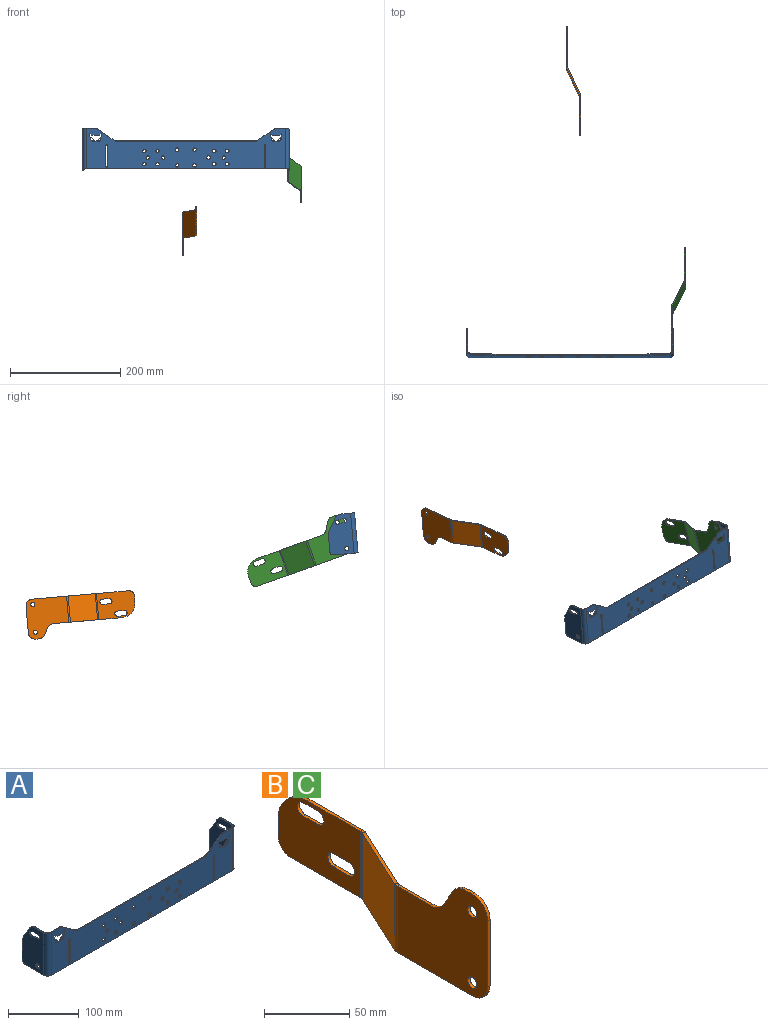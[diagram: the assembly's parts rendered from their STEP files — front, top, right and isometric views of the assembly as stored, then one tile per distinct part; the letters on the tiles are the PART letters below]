
ASSEMBLY  parts=3 mates=1
PART A: 94 faces, bbox 375.8x50.8x73 mm
  f0: cylinder r=4.27mm len=6.04mm, axis (0,-1,0), area 20.5mm2, adj f55,f56,f57
  f1: cylinder r=4.27mm len=6.04mm, axis (0,-1,0), area 20.5mm2, adj f54,f56,f57
  f2: cylinder r=6.35mm len=3.64mm, axis (0,-1,0), area 7.7mm2, adj f3,f53,f56,f57
  f3: plane 28.46x19.93mm, normal (-0.57,0,0.82), area 68.8mm2, adj f2,f4,f56,f57
  f4: cylinder r=6.35mm len=3.64mm, axis (0,-1,0), area 7.7mm2, adj f3,f5,f56,f57
  f5: plane 18.32x1.98mm, normal (0,0,1), area 36.3mm2, adj f4,f56,f57,f72
  f6: plane 361.68x1.98mm, normal (0,0,-1), area 716.6mm2, adj f56,f57,f73,f90
  f7: plane 18.32x1.98mm, normal (0,0,1), area 36.3mm2, adj f8,f56,f57,f91
  f8: cylinder r=6.35mm len=3.64mm, axis (0,-1,0), area 7.7mm2, adj f7,f9,f56,f57
  f9: plane 28.46x19.93mm, normal (0.57,0,0.82), area 68.8mm2, adj f8,f10,f56,f57
  f10: cylinder r=6.35mm len=3.64mm, axis (0,-1,0), area 7.7mm2, adj f9,f53,f56,f57
  f11: plane 5.66x5.66mm, normal (0.71,0,-0.71), area 15.8mm2, adj f36,f56,f57
  f12: plane 5x1.98mm, normal (-1,0,0), area 9.9mm2, adj f13,f35,f56,f57
  f13: plane 3.54x3.54mm, normal (0.71,0,-0.71), area 9.9mm2, adj f12,f14,f56,f57
  f14: plane 14.14x1.98mm, normal (0,0,-1), area 28mm2, adj f13,f15,f56,f57
  f15: plane 3.54x3.54mm, normal (-0.71,0,-0.71), area 9.9mm2, adj f14,f16,f56,f57
  f16: plane 5x1.98mm, normal (1,0,0), area 9.9mm2, adj f15,f17,f56,f57
  f17: plane 10.61x10.61mm, normal (0.71,0,0.71), area 29.7mm2, adj f16,f35,f56,f57
  f18: plane 5.66x5.66mm, normal (0.71,0,-0.71), area 15.8mm2, adj f34,f56,f57
  f19: plane 5x1.98mm, normal (-1,0,0), area 9.9mm2, adj f20,f33,f56,f57
  f20: plane 3.54x3.54mm, normal (0.71,0,-0.71), area 9.9mm2, adj f19,f21,f56,f57
  f21: plane 14.14x1.98mm, normal (0,0,-1), area 28mm2, adj f20,f22,f56,f57
  f22: plane 3.54x3.54mm, normal (-0.71,0,-0.71), area 9.9mm2, adj f21,f23,f56,f57
  f23: plane 5x1.98mm, normal (1,0,0), area 9.9mm2, adj f22,f24,f56,f57
  f24: plane 10.61x10.61mm, normal (0.71,0,0.71), area 29.7mm2, adj f23,f33,f56,f57
  f25: cylinder r=1.59mm len=3.18mm, axis (0,-1,0), area 9.9mm2, adj f26,f32,f56,f57
  f26: plane 38.1x1.98mm, normal (-1,0,0), area 75.5mm2, adj f25,f27,f56,f57
  f27: cylinder r=1.59mm len=3.18mm, axis (0,-1,0), area 9.9mm2, adj f26,f32,f56,f57
  f28: cylinder r=1.59mm len=3.18mm, axis (0,-1,0), area 9.9mm2, adj f29,f31,f56,f57
  f29: plane 38.1x1.98mm, normal (-1,0,0), area 75.5mm2, adj f28,f30,f56,f57
  f30: cylinder r=1.59mm len=3.18mm, axis (0,-1,0), area 9.9mm2, adj f29,f31,f56,f57
  f31: plane 38.1x1.98mm, normal (1,0,0), area 75.5mm2, adj f28,f30,f56,f57
  f32: plane 38.1x1.98mm, normal (1,0,0), area 75.5mm2, adj f25,f27,f56,f57
  f33: plane 10.61x10.61mm, normal (-0.71,0,0.71), area 29.7mm2, adj f19,f24,f56,f57
  f34: cylinder r=4.27mm len=6.04mm, axis (0,-1,0), area 20.5mm2, adj f18,f56,f57
  f35: plane 10.61x10.61mm, normal (-0.71,0,0.71), area 29.7mm2, adj f12,f17,f56,f57
  f36: cylinder r=4.27mm len=6.04mm, axis (0,-1,0), area 20.5mm2, adj f11,f56,f57
  f37: cylinder r=3.17mm len=6.35mm, axis (0,-1,0), area 39.5mm2, adj f56,f57
  f38: cylinder r=3.17mm len=6.35mm, axis (0,-1,0), area 39.5mm2, adj f56,f57
  f39: cylinder r=3.17mm len=6.35mm, axis (0,-1,0), area 39.5mm2, adj f56,f57
  f40: cylinder r=3.17mm len=6.35mm, axis (0,-1,0), area 39.5mm2, adj f56,f57
  f41: cylinder r=3.17mm len=6.35mm, axis (0,-1,0), area 39.5mm2, adj f56,f57
  f42: cylinder r=3.17mm len=6.35mm, axis (0,-1,0), area 39.5mm2, adj f56,f57
  f43: cylinder r=3.17mm len=6.35mm, axis (0,-1,0), area 39.5mm2, adj f56,f57
  f44: cylinder r=3.17mm len=6.35mm, axis (0,-1,0), area 39.5mm2, adj f56,f57
  f45: cylinder r=3.17mm len=6.35mm, axis (0,-1,0), area 39.5mm2, adj f56,f57
  f46: cylinder r=3.17mm len=6.35mm, axis (0,-1,0), area 39.5mm2, adj f56,f57
  f47: cylinder r=3.17mm len=6.35mm, axis (0,-1,0), area 39.5mm2, adj f56,f57
  f48: cylinder r=3.17mm len=6.35mm, axis (0,-1,0), area 39.5mm2, adj f56,f57
  f49: cylinder r=3.17mm len=6.35mm, axis (0,-1,0), area 39.5mm2, adj f56,f57
  f50: cylinder r=3.17mm len=6.35mm, axis (0,-1,0), area 39.5mm2, adj f56,f57
  f51: cylinder r=3.17mm len=6.35mm, axis (0,-1,0), area 39.5mm2, adj f56,f57
  f52: cylinder r=3.17mm len=6.35mm, axis (0,-1,0), area 39.5mm2, adj f56,f57
  f53: plane 253.56x1.98mm, normal (0,0,1), area 502.3mm2, adj f2,f10,f56,f57
  f54: plane 5.66x5.66mm, normal (-0.71,0,-0.71), area 15.8mm2, adj f1,f56,f57
  f55: plane 5.66x5.66mm, normal (-0.71,0,-0.71), area 15.8mm2, adj f0,f56,f57
  f56: plane 361.68x73.03mm, normal (0,1,0), area 18841.1mm2, adj f0,f1,f2,f3,f4,f5,f6,f7
  f57: plane 361.68x73.03mm, normal (0,-1,0), area 18841.1mm2, adj f0,f1,f2,f3,f4,f5,f6,f7
  f58: plane 33.22x1.98mm, normal (0,1,0), area 65.8mm2, adj f67,f68,f69,f70
  f59: plane 37.39x1.98mm, normal (0,0,-1), area 74.1mm2, adj f67,f68,f69,f73
  f60: plane 18.08x1.98mm, normal (0,0,1), area 35.8mm2, adj f67,f68,f71,f72
  f61: cylinder r=3.81mm len=7.42mm, axis (-1,0,0), area 23.8mm2, adj f62,f65,f67,f68
  f62: cylinder r=35.1mm len=14.13mm, axis (-1,0,0), area 28.4mm2, adj f61,f63,f67,f68
  f63: cylinder r=3.81mm len=7.61mm, axis (-1,0,0), area 23.8mm2, adj f62,f65,f67,f68
  f64: cylinder r=3.81mm len=7.62mm, axis (-1,0,0), area 47.4mm2, adj f67,f68
  f65: cylinder r=26.75mm len=11.03mm, axis (-1,0,0), area 22.2mm2, adj f61,f63,f67,f68
  f66: plane 23.93x13.81mm, normal (0,0.87,0.5), area 54.7mm2, adj f67,f68,f70,f71
  f67: plane 73.03x43.74mm, normal (-1,0,0), area 2696.9mm2, adj f58,f59,f60,f61,f62,f63,f64,f65
  f68: plane 73.03x43.74mm, normal (1,0,0), area 2696.9mm2, adj f58,f59,f60,f61,f62,f63,f64,f65
  f69: cylinder r=6.35mm len=6.35mm, axis (-1,0,0), area 19.8mm2, adj f58,f59,f67,f68
  f70: cylinder r=6.35mm len=3.18mm, axis (1,0,0), area 6.6mm2, adj f58,f66,f67,f68
  f71: cylinder r=12.7mm len=11mm, axis (1,0,0), area 26.3mm2, adj f60,f66,f67,f68
  f72: plane 7.06x7.06mm, normal (0,0,1), area 18.9mm2, adj f5,f60,f74,f75
  f73: plane 7.06x7.06mm, normal (0,0,-1), area 18.9mm2, adj f6,f59,f74,f75
  f74: cylinder r=7.06mm len=73.03mm, axis (0,0,1), area 810mm2, adj f57,f68,f72,f73
  f75: cylinder r=5.08mm len=73.03mm, axis (0,0,1), area 582.7mm2, adj f56,f67,f72,f73
  f76: cylinder r=3.81mm len=7.42mm, axis (1,0,0), area 23.8mm2, adj f77,f84,f85,f86
  f77: cylinder r=26.75mm len=11.03mm, axis (1,0,0), area 22.2mm2, adj f76,f78,f85,f86
  f78: cylinder r=3.81mm len=7.61mm, axis (1,0,0), area 23.8mm2, adj f77,f84,f85,f86
  f79: plane 37.39x1.98mm, normal (0,0,-1), area 74.1mm2, adj f85,f86,f87,f90
  f80: plane 33.22x1.98mm, normal (0,1,0), area 65.8mm2, adj f85,f86,f87,f89
  f81: plane 23.93x13.81mm, normal (0,0.87,0.5), area 54.7mm2, adj f85,f86,f88,f89
  f82: plane 18.08x1.98mm, normal (0,0,1), area 35.8mm2, adj f85,f86,f88,f91
  f83: cylinder r=3.81mm len=7.62mm, axis (1,0,0), area 47.4mm2, adj f85,f86
  f84: cylinder r=35.1mm len=14.13mm, axis (1,0,0), area 28.4mm2, adj f76,f78,f85,f86
  f85: plane 73.03x43.74mm, normal (1,0,0), area 2696.9mm2, adj f76,f77,f78,f79,f80,f81,f82,f83
  f86: plane 73.03x43.74mm, normal (-1,0,0), area 2696.9mm2, adj f76,f77,f78,f79,f80,f81,f82,f83
  f87: cylinder r=6.35mm len=6.35mm, axis (1,0,0), area 19.8mm2, adj f79,f80,f85,f86
  f88: cylinder r=12.7mm len=11mm, axis (1,0,0), area 26.3mm2, adj f81,f82,f85,f86
  f89: cylinder r=6.35mm len=3.18mm, axis (1,0,0), area 6.6mm2, adj f80,f81,f85,f86
  f90: plane 7.06x7.06mm, normal (0,0,-1), area 18.9mm2, adj f6,f79,f92,f93
  f91: plane 7.06x7.06mm, normal (0,0,1), area 18.9mm2, adj f7,f82,f92,f93
  f92: cylinder r=7.06mm len=73.03mm, axis (0,0,-1), area 810mm2, adj f57,f86,f90,f91
  f93: cylinder r=5.08mm len=73.03mm, axis (0,0,-1), area 582.7mm2, adj f56,f85,f90,f91
PART B: 40 faces, bbox 26.1x197.8x73 mm
  f0: plane 27.68x1.98mm, normal (0,0,1), area 54.8mm2, adj f7,f8,f12,f36
  f1: plane 62.37x1.98mm, normal (0,0,-1), area 123.6mm2, adj f7,f8,f9,f37
  f2: plane 47.63x1.98mm, normal (0,-1,0), area 94.4mm2, adj f7,f8,f9,f10
  f3: plane 5.37x1.98mm, normal (0,0,1), area 10.6mm2, adj f7,f8,f10,f11
  f4: cylinder r=3.81mm len=7.62mm, axis (1,0,0), area 47.4mm2, adj f7,f8
  f5: cylinder r=3.81mm len=7.62mm, axis (1,0,0), area 47.4mm2, adj f7,f8
  f6: plane 12.7x7.33mm, normal (0,0.87,0.5), area 29.1mm2, adj f7,f8,f11,f12
  f7: plane 75.07x73.03mm, normal (-1,0,0), area 4246.4mm2, adj f0,f1,f2,f3,f4,f5,f6,f9
  f8: plane 75.07x73.03mm, normal (1,0,0), area 4246.4mm2, adj f0,f1,f2,f3,f4,f5,f6,f9
  f9: cylinder r=12.7mm len=12.7mm, axis (-1,0,0), area 39.5mm2, adj f1,f2,f7,f8
  f10: cylinder r=12.7mm len=12.7mm, axis (1,0,0), area 39.5mm2, adj f2,f3,f7,f8
  f11: cylinder r=12.7mm len=11mm, axis (-1,0,0), area 26.3mm2, adj f3,f6,f7,f8
  f12: cylinder r=12.7mm len=11mm, axis (-1,0,0), area 26.3mm2, adj f0,f6,f7,f8
  f13: plane 50.19x24.81mm, normal (0,0,-1), area 107.9mm2, adj f15,f16,f32,f37
  f14: plane 50.19x24.81mm, normal (0,0,1), area 107.9mm2, adj f15,f16,f33,f36
  f15: plane 49.36x47.63mm, normal (-0.91,0.42,0), area 2593.6mm2, adj f13,f14,f35,f38
  f16: plane 49.36x47.63mm, normal (0.91,-0.42,0), area 2593.6mm2, adj f13,f14,f34,f39
  f17: cylinder r=4.76mm len=9.53mm, axis (-1,0,0), area 29.6mm2, adj f18,f27,f28,f29
  f18: plane 12.7x1.98mm, normal (0,0,1), area 25.2mm2, adj f17,f19,f28,f29
  f19: cylinder r=4.76mm len=9.53mm, axis (-1,0,0), area 29.6mm2, adj f18,f27,f28,f29
  f20: cylinder r=4.76mm len=9.53mm, axis (-1,0,0), area 29.6mm2, adj f21,f26,f28,f29
  f21: plane 12.7x1.98mm, normal (0,0,1), area 25.2mm2, adj f20,f22,f28,f29
  f22: cylinder r=4.76mm len=9.53mm, axis (-1,0,0), area 29.6mm2, adj f21,f26,f28,f29
  f23: plane 12.07x1.98mm, normal (0,1,0), area 23.9mm2, adj f28,f29,f30,f31
  f24: plane 58.12x1.98mm, normal (0,0,-1), area 115.2mm2, adj f28,f29,f30,f32
  f25: plane 42.88x1.98mm, normal (0,0,1), area 85mm2, adj f28,f29,f31,f33
  f26: plane 12.7x1.98mm, normal (0,0,-1), area 25.2mm2, adj f20,f22,f28,f29
  f27: plane 12.7x1.98mm, normal (0,0,-1), area 25.2mm2, adj f17,f19,f28,f29
  f28: plane 68.28x47.63mm, normal (-1,0,0), area 2707mm2, adj f17,f18,f19,f20,f21,f22,f23,f24
  f29: plane 68.28x47.63mm, normal (1,0,0), area 2707mm2, adj f17,f18,f19,f20,f21,f22,f23,f24
  f30: cylinder r=10.16mm len=10.16mm, axis (-1,0,0), area 31.6mm2, adj f23,f24,f28,f29
  f31: cylinder r=25.4mm len=25.4mm, axis (-1,0,0), area 79mm2, adj f23,f25,f28,f29
  f32: plane 2.98x2.46mm, normal (0,0,-1), area 5.2mm2, adj f13,f24,f34,f35
  f33: plane 2.98x2.46mm, normal (0,0,1), area 5.2mm2, adj f14,f25,f34,f35
  f34: cylinder r=7.06mm len=47.63mm, axis (0,0,-1), area 146.7mm2, adj f16,f29,f32,f33
  f35: cylinder r=5.08mm len=47.63mm, axis (0,0,-1), area 105.6mm2, adj f15,f28,f32,f33
  f36: plane 2.98x2.46mm, normal (0,0,1), area 5.2mm2, adj f0,f14,f38,f39
  f37: plane 2.98x2.46mm, normal (0,0,-1), area 5.2mm2, adj f1,f13,f38,f39
  f38: cylinder r=7.06mm len=47.63mm, axis (0,0,1), area 146.7mm2, adj f7,f15,f36,f37
  f39: cylinder r=5.08mm len=47.63mm, axis (0,0,1), area 105.6mm2, adj f8,f16,f36,f37
PART C: same geometry as B
PLACE A rot(axis=(-1,0,0),5deg) t=(40.55,-49.29,-92.79)mm
PLACE B rot(axis=(1,0,0),175deg) t=(-71.96,512.35,-218.59)mm
PLACE C rot(axis=(-1,0,0),19.8deg) t=(118.1,-7.21,-111.12)mm
MATE revolute C.f4 <-> A.f83  axis (1,0,0) through (120.08,-33.02,-110.83)mm
